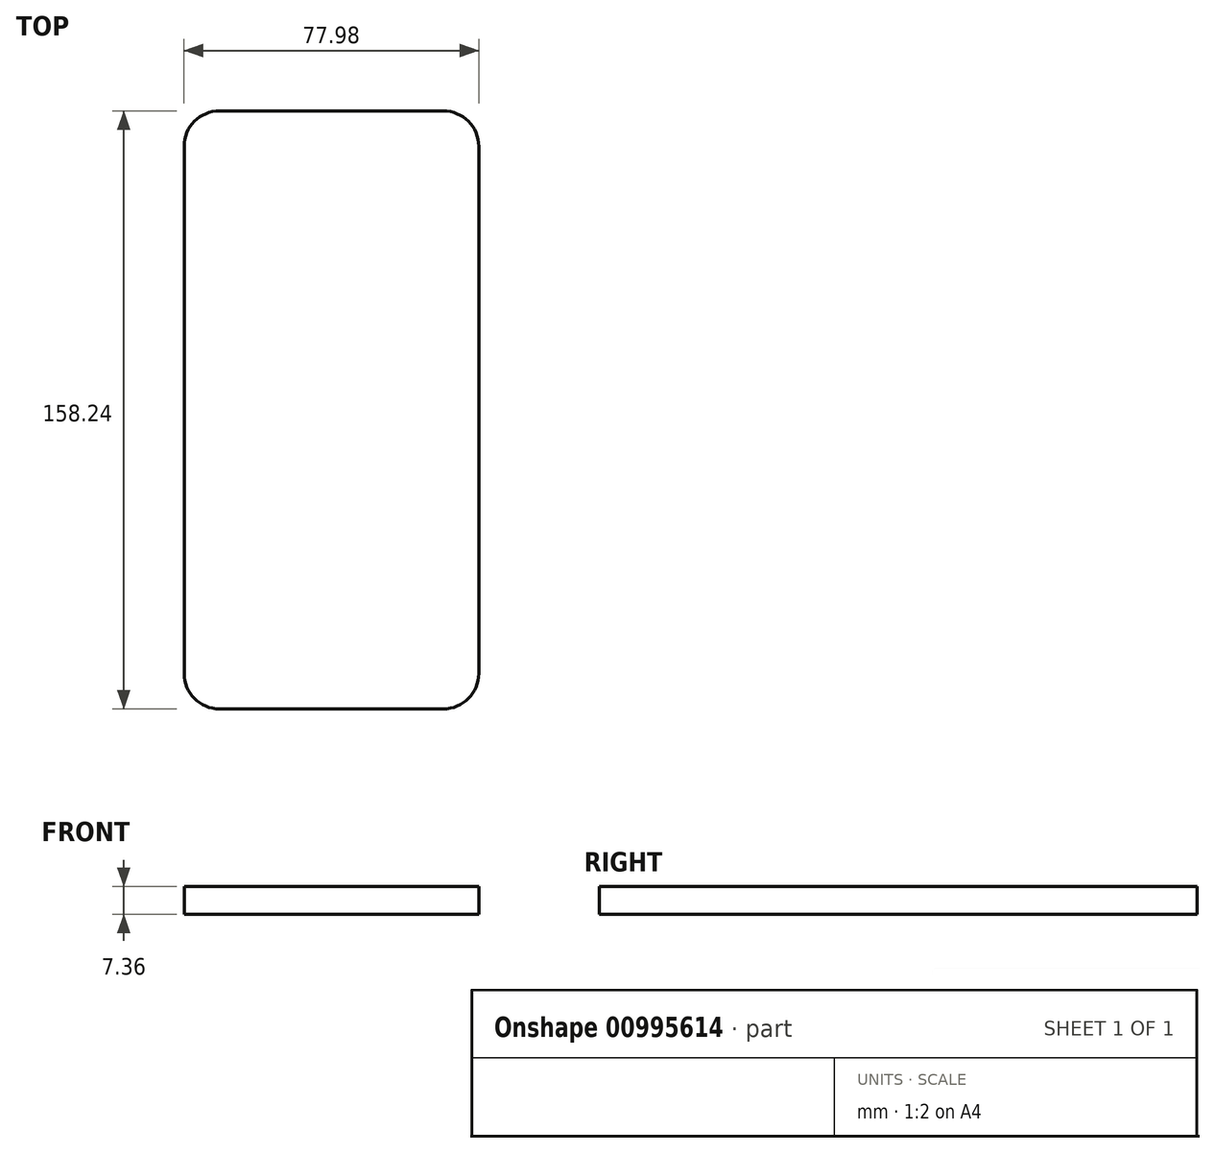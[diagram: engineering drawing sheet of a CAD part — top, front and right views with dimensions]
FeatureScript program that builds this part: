
annotation { "Feature Type Name" : "Feature", "Feature Type Description" : "" }
export const myFeature = defineFeature(function(context is Context, id is Id, definition is map)
    precondition{}
    {
        {
            var Q0;
            Q0=qCreatedBy(makeId("Top.planeOp"),FACE);
            var sketch = newSketch(context, id + "F0", { "sketchPlane" : qUnion([Q0])});
            skLineSegment(sketch, "E0.bottom", {"start": v(38.99, -79.12) * mm, "end": v(-38.99, -79.12) * mm});
            skLineSegment(sketch, "E0.top", {"start": v(38.99, 79.12) * mm, "end": v(-38.99, 79.12) * mm});
            skLineSegment(sketch, "E0.left", {"start": v(38.99, -79.12) * mm, "end": v(38.99, 79.12) * mm});
            skLineSegment(sketch, "E0.right", {"start": v(-38.99, -79.12) * mm, "end": v(-38.99, 79.12) * mm});
            skPoint(sketch, "E0.middle", {"position": v(0, 0) * mm});
            skSolve(sketch);
        }
        {
            var Q0;
            Q0 = qSketchRegion(id + "F0", true);
            extrude(context, id + "F1", {"entities" : qUnion([Q0]), "endBound" : BoundingType.SYMMETRIC, "depth" : 7.37 * mm, "offsetDistance" : 25.4 * mm});
        }
        {
            var Q0;
            Q0=makeQuery(id+"F1.opExtrude","SWEPT_EDGE",EDGE,{"disambiguationData":[OSD([sQuery(id+"F0.wireOp",EDGE,"E0.top"),sQuery(id+"F0.wireOp",EDGE,"E0.right")])]});
            var Q1;
            Q1=makeQuery(id+"F1.opExtrude","SWEPT_EDGE",EDGE,{"disambiguationData":[OSD([sQuery(id+"F0.wireOp",EDGE,"E0.top"),sQuery(id+"F0.wireOp",EDGE,"E0.left")])]});
            var Q2;
            Q2=makeQuery(id+"F1.opExtrude","SWEPT_EDGE",EDGE,{"disambiguationData":[OSD([sQuery(id+"F0.wireOp",EDGE,"E0.bottom"),sQuery(id+"F0.wireOp",EDGE,"E0.left")])]});
            var Q3;
            Q3=makeQuery(id+"F1.opExtrude","SWEPT_EDGE",EDGE,{"disambiguationData":[OSD([sQuery(id+"F0.wireOp",EDGE,"E0.bottom"),sQuery(id+"F0.wireOp",EDGE,"E0.right")])]});
            fillet(context, id + "F2", {"entities" : qUnion([Q0, Q1, Q2, Q3]), "radius" : 9.37 * mm, "tangentPropagation" : true, "allowEdgeOverflow" : false});
        }
    });
